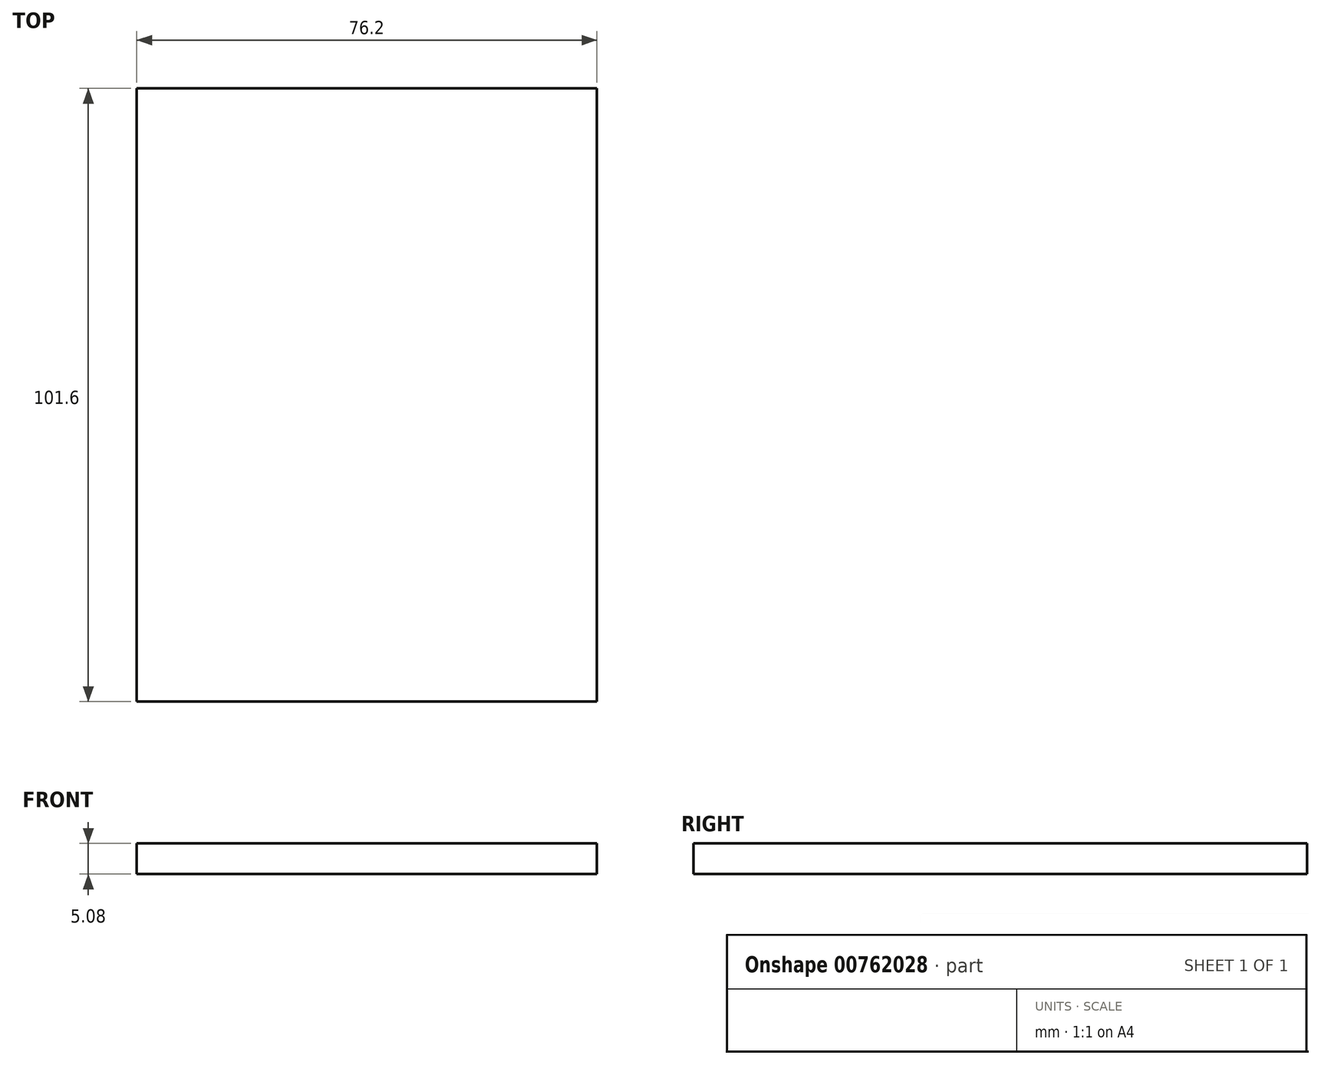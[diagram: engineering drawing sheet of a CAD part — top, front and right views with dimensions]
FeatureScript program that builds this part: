
annotation { "Feature Type Name" : "Feature", "Feature Type Description" : "" }
export const myFeature = defineFeature(function(context is Context, id is Id, definition is map)
    precondition{}
    {
        {
            var Q0;
            Q0=qCreatedBy(makeId("Top.planeOp"),FACE);
            var sketch = newSketch(context, id + "F0", { "sketchPlane" : qUnion([Q0])});
            skLineSegment(sketch, "E0.bottom", {"start": v(-67.27, 59.74) * mm, "end": v(8.93, 59.74) * mm});
            skLineSegment(sketch, "E0.top", {"start": v(-67.27, -41.86) * mm, "end": v(8.93, -41.86) * mm});
            skLineSegment(sketch, "E0.left", {"start": v(-67.27, 59.74) * mm, "end": v(-67.27, -41.86) * mm});
            skLineSegment(sketch, "E0.right", {"start": v(8.93, 59.74) * mm, "end": v(8.93, -41.86) * mm});
            skSolve(sketch);
        }
        {
            var Q0;
            Q0=makeQuery(id+"F0.imprint","IMPRINT",FACE,{"disambiguationData":[TD([[makeQuery(id+"F0.imprint","IMPRINT",EDGE,{"derivedFrom":sQuery(id+"F0.wireOp",EDGE,"E0.bottom")}),-1.0]])]});
            extrude(context, id + "F1", {"entities" : qUnion([Q0]), "depth" : 5.08 * mm, "offsetDistance" : 25.4 * mm});
        }
    });
